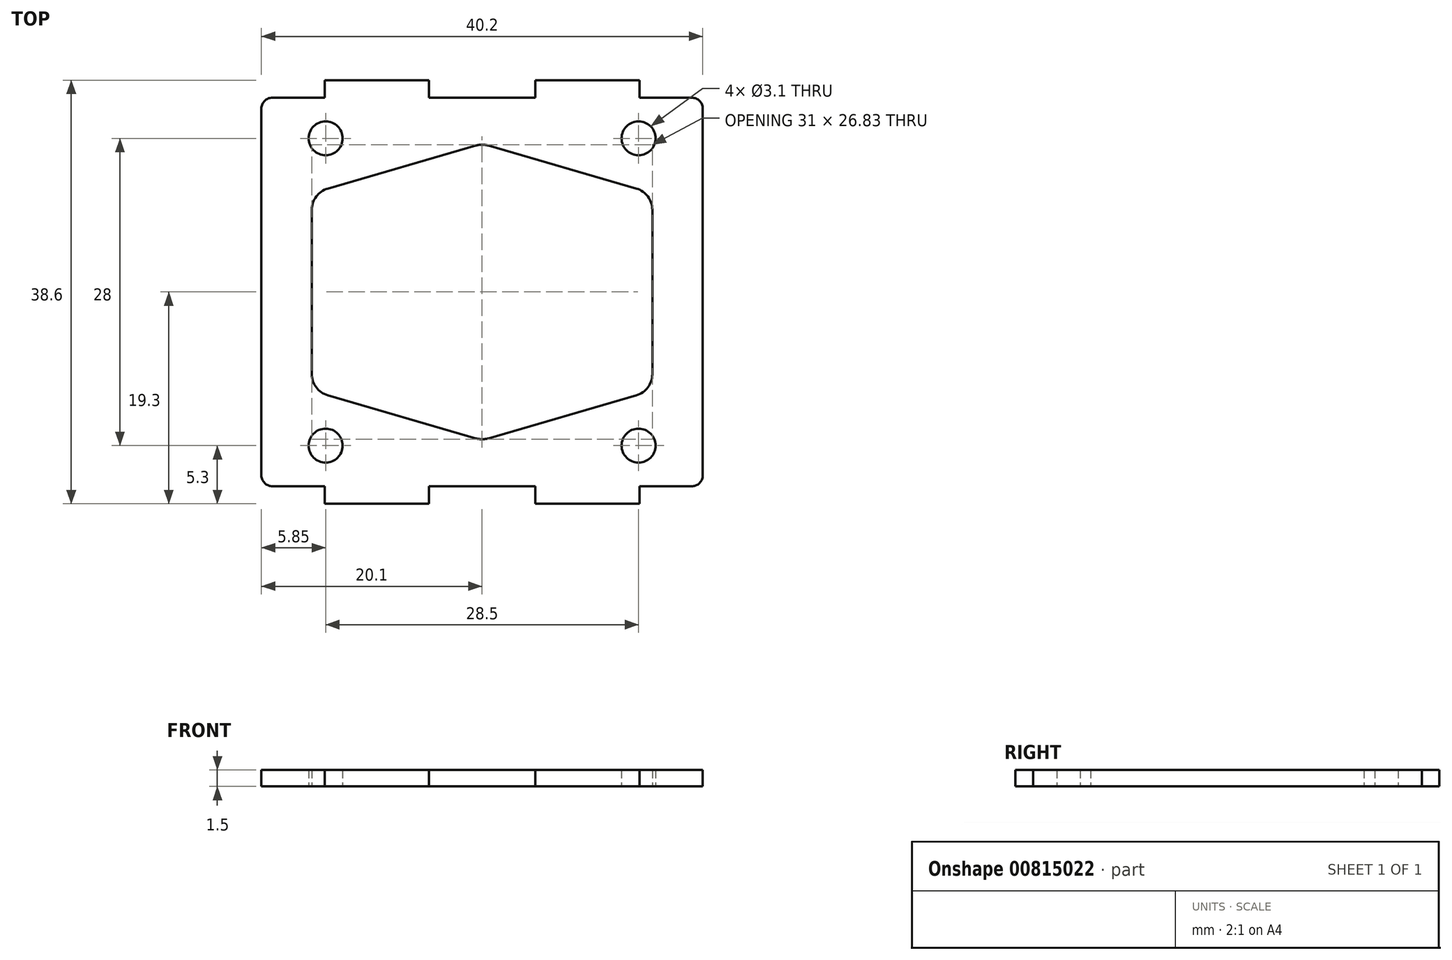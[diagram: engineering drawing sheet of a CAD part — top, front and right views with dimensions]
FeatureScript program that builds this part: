
annotation { "Feature Type Name" : "Feature", "Feature Type Description" : "" }
export const myFeature = defineFeature(function(context is Context, id is Id, definition is map)
    precondition{}
    {
        {
            var Q0;
            Q0=qCreatedBy(makeId("Top.planeOp"),FACE);
            var sketch = newSketch(context, id + "F0", { "sketchPlane" : qUnion([Q0])});
            skLineSegment(sketch, "E0.0", {"start": v(-20.1, 17.7) * mm, "end": v(-20.1, -17.7) * mm});
            skLineSegment(sketch, "E1.0", {"start": v(-14.33, 17.7) * mm, "end": v(-20.1, 17.7) * mm});
            skLineSegment(sketch, "E2.0", {"start": v(-14.33, 19.3) * mm, "end": v(-14.33, 17.7) * mm});
            skLineSegment(sketch, "E3.0", {"start": v(-4.85, 19.3) * mm, "end": v(-14.33, 19.3) * mm});
            skLineSegment(sketch, "E4.0", {"start": v(-4.85, 17.7) * mm, "end": v(-4.85, 19.3) * mm});
            skLineSegment(sketch, "E5.0", {"start": v(0, 17.7) * mm, "end": v(-4.85, 17.7) * mm});
            skLineSegment(sketch, "E6.0", {"start": v(0, 13.5) * mm, "end": v(-15.5, 9) * mm});
            skLineSegment(sketch, "E7.0", {"start": v(-15.5, 9) * mm, "end": v(-15.5, -9) * mm});
            skLineSegment(sketch, "E8.0", {"start": v(-15.5, -9) * mm, "end": v(0, -13.5) * mm});
            skLineSegment(sketch, "E9.0", {"start": v(-20.1, -17.7) * mm, "end": v(-14.33, -17.7) * mm});
            skLineSegment(sketch, "E10.0", {"start": v(-14.33, -17.7) * mm, "end": v(-14.33, -19.3) * mm});
            skLineSegment(sketch, "E11.0", {"start": v(-14.33, -19.3) * mm, "end": v(-4.85, -19.3) * mm});
            skLineSegment(sketch, "E12.0", {"start": v(-4.85, -19.3) * mm, "end": v(-4.85, -17.7) * mm});
            skLineSegment(sketch, "E13.0", {"start": v(-4.85, -17.7) * mm, "end": v(0, -17.7) * mm});
            skLineSegment(sketch, "E14", {"start": v(0, 17.7) * mm, "end": v(0, -17.7) * mm, "construction": true});
            skLineSegment(sketch, "E15", {"start": v(-20.1, 0) * mm, "end": v(22.62, 0) * mm, "construction": true});
            skLineSegment(sketch, "E16.bottom", {"start": v(14.25, -14) * mm, "end": v(-14.25, -14) * mm, "construction": true});
            skLineSegment(sketch, "E16.top", {"start": v(14.25, 14) * mm, "end": v(-14.25, 14) * mm, "construction": true});
            skLineSegment(sketch, "E16.left", {"start": v(14.25, -14) * mm, "end": v(14.25, 14) * mm, "construction": true});
            skLineSegment(sketch, "E16.right", {"start": v(-14.25, -14) * mm, "end": v(-14.25, 14) * mm, "construction": true});
            skPoint(sketch, "E16.middle", {"position": v(0, 0) * mm});
            skCircle(sketch, "E17", {"center": v(-14.25, 14) * mm, "radius": 1.55 * mm});
            skCircle(sketch, "E18", {"center": v(-14.25, -14) * mm, "radius": 1.55 * mm});
            skLineSegment(sketch, "E19.MirrorCS", {"start": v(0, 17.7) * mm, "end": v(4.85, 17.7) * mm});
            skLineSegment(sketch, "E20.MirrorCS", {"start": v(4.85, 17.7) * mm, "end": v(4.85, 19.3) * mm});
            skLineSegment(sketch, "E21.MirrorCS", {"start": v(4.85, 19.3) * mm, "end": v(14.33, 19.3) * mm});
            skLineSegment(sketch, "E22.MirrorCS", {"start": v(14.33, 19.3) * mm, "end": v(14.33, 17.7) * mm});
            skLineSegment(sketch, "E23.MirrorCS", {"start": v(14.33, 17.7) * mm, "end": v(20.1, 17.7) * mm});
            skLineSegment(sketch, "E24.MirrorCS", {"start": v(20.1, 17.7) * mm, "end": v(20.1, -17.7) * mm});
            skLineSegment(sketch, "E25.MirrorCS", {"start": v(20.1, -17.7) * mm, "end": v(14.33, -17.7) * mm});
            skLineSegment(sketch, "E26.MirrorCS", {"start": v(14.33, -17.7) * mm, "end": v(14.33, -19.3) * mm});
            skLineSegment(sketch, "E27.MirrorCS", {"start": v(14.33, -19.3) * mm, "end": v(4.85, -19.3) * mm});
            skLineSegment(sketch, "E28.MirrorCS", {"start": v(4.85, -19.3) * mm, "end": v(4.85, -17.7) * mm});
            skLineSegment(sketch, "E29.MirrorCS", {"start": v(4.85, -17.7) * mm, "end": v(0, -17.7) * mm});
            skCircle(sketch, "E30.MirrorC", {"center": v(14.25, -14) * mm, "radius": 1.55 * mm});
            skCircle(sketch, "E31.MirrorC", {"center": v(14.25, 14) * mm, "radius": 1.55 * mm});
            skLineSegment(sketch, "E32.MirrorCS", {"start": v(0, 13.5) * mm, "end": v(15.5, 9) * mm});
            skLineSegment(sketch, "E33.MirrorCS", {"start": v(15.5, 9) * mm, "end": v(15.5, -9) * mm});
            skLineSegment(sketch, "E34.MirrorCS", {"start": v(15.5, -9) * mm, "end": v(0, -13.5) * mm});
            skSolve(sketch);
        }
        {
            var Q0;
            Q0=makeQuery(id+"F0.imprint","IMPRINT",FACE,{"disambiguationData":[TD([[makeQuery(id+"F0.imprint","IMPRINT",EDGE,{"derivedFrom":sQuery(id+"F0.wireOp",EDGE,"E0.0")}),1.0]])]});
            extrude(context, id + "F1", {"entities" : qUnion([Q0]), "depth" : 1.5 * mm, "offsetDistance" : 25 * mm});
        }
        {
            var Q0;
            Q0=makeQuery(id+"F1.opExtrude","SWEPT_EDGE",EDGE,{"disambiguationData":[OSD([sQuery(id+"F0.wireOp",EDGE,"E7.0"),sQuery(id+"F0.wireOp",EDGE,"E8.0")])]});
            var Q1;
            Q1=makeQuery(id+"F1.opExtrude","SWEPT_EDGE",EDGE,{"disambiguationData":[OSD([sQuery(id+"F0.wireOp",EDGE,"E6.0"),sQuery(id+"F0.wireOp",EDGE,"E7.0")])]});
            var Q2;
            Q2=makeQuery(id+"F1.opExtrude","SWEPT_EDGE",EDGE,{"disambiguationData":[OSD([sQuery(id+"F0.wireOp",EDGE,"E6.0"),sQuery(id+"F0.wireOp",EDGE,"E32.MirrorCS")])]});
            var Q3;
            Q3=makeQuery(id+"F1.opExtrude","SWEPT_EDGE",EDGE,{"disambiguationData":[OSD([sQuery(id+"F0.wireOp",EDGE,"E32.MirrorCS"),sQuery(id+"F0.wireOp",EDGE,"E33.MirrorCS")])]});
            var Q4;
            Q4=makeQuery(id+"F1.opExtrude","SWEPT_EDGE",EDGE,{"disambiguationData":[OSD([sQuery(id+"F0.wireOp",EDGE,"E33.MirrorCS"),sQuery(id+"F0.wireOp",EDGE,"E34.MirrorCS")])]});
            var Q5;
            Q5=makeQuery(id+"F1.opExtrude","SWEPT_EDGE",EDGE,{"disambiguationData":[OSD([sQuery(id+"F0.wireOp",EDGE,"E8.0"),sQuery(id+"F0.wireOp",EDGE,"E34.MirrorCS")])]});
            fillet(context, id + "F2", {"entities" : qUnion([Q0, Q1, Q2, Q3, Q4, Q5]), "radius" : 2 * mm, "tangentPropagation" : true, "allowEdgeOverflow" : false});
        }
        {
            var Q0;
            Q0=makeQuery(id+"F1.opExtrude","SWEPT_EDGE",EDGE,{"disambiguationData":[OSD([sQuery(id+"F0.wireOp",EDGE,"E0.0"),sQuery(id+"F0.wireOp",EDGE,"E1.0")])]});
            var Q1;
            Q1=makeQuery(id+"F1.opExtrude","SWEPT_EDGE",EDGE,{"disambiguationData":[OSD([sQuery(id+"F0.wireOp",EDGE,"E23.MirrorCS"),sQuery(id+"F0.wireOp",EDGE,"E24.MirrorCS")])]});
            var Q2;
            Q2=makeQuery(id+"F1.opExtrude","SWEPT_EDGE",EDGE,{"disambiguationData":[OSD([sQuery(id+"F0.wireOp",EDGE,"E24.MirrorCS"),sQuery(id+"F0.wireOp",EDGE,"E25.MirrorCS")])]});
            var Q3;
            Q3=makeQuery(id+"F1.opExtrude","SWEPT_EDGE",EDGE,{"disambiguationData":[OSD([sQuery(id+"F0.wireOp",EDGE,"E0.0"),sQuery(id+"F0.wireOp",EDGE,"E9.0")])]});
            fillet(context, id + "F3", {"entities" : qUnion([Q0, Q1, Q2, Q3]), "radius" : 1 * mm, "tangentPropagation" : true, "allowEdgeOverflow" : false});
        }
    });
